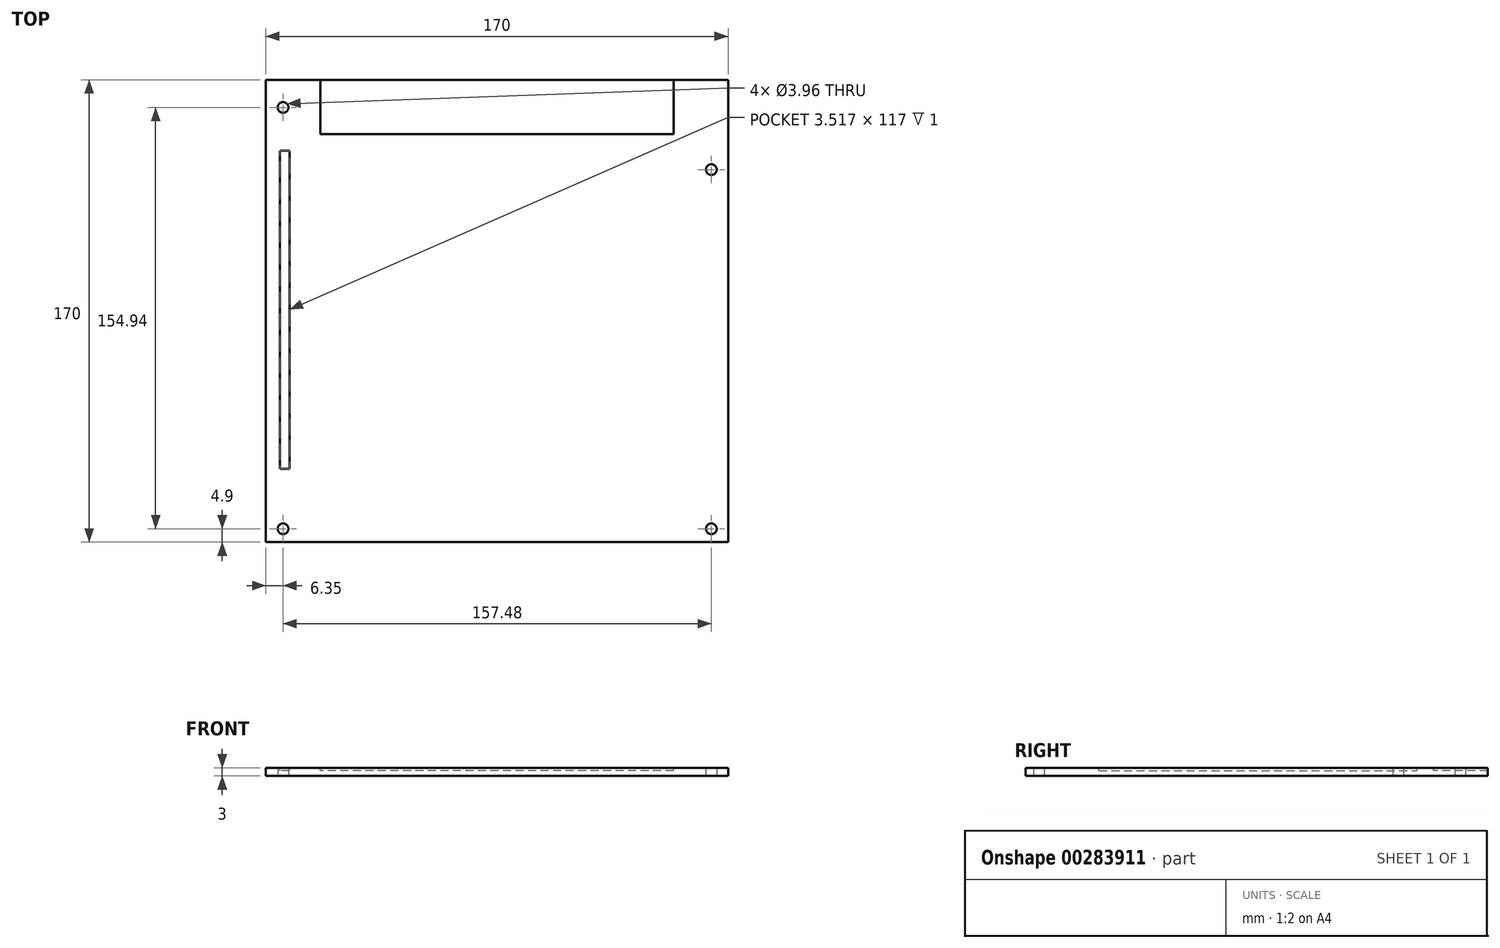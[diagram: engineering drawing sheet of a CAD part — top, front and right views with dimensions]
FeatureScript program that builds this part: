
annotation { "Feature Type Name" : "Feature", "Feature Type Description" : "" }
export const myFeature = defineFeature(function(context is Context, id is Id, definition is map)
    precondition{}
    {
        {
            var Q0;
            Q0=qCreatedBy(makeId("Top.planeOp"),FACE);
            var sketch = newSketch(context, id + "F0", { "sketchPlane" : qUnion([Q0])});
            skLineSegment(sketch, "E0.bottom", {"start": v(85, 85) * mm, "end": v(-85, 85) * mm});
            skLineSegment(sketch, "E0.top", {"start": v(85, -85) * mm, "end": v(-85, -85) * mm});
            skLineSegment(sketch, "E0.left", {"start": v(85, 85) * mm, "end": v(85, -85) * mm});
            skLineSegment(sketch, "E0.right", {"start": v(-85, 85) * mm, "end": v(-85, -85) * mm});
            skPoint(sketch, "E0.middle", {"position": v(0, 0) * mm});
            skCircle(sketch, "E1", {"center": v(-78.65, 74.84) * mm, "radius": 1.98 * mm});
            skCircle(sketch, "E2", {"center": v(78.83, 51.98) * mm, "radius": 1.98 * mm});
            skCircle(sketch, "E3", {"center": v(-78.65, -80.1) * mm, "radius": 1.98 * mm});
            skCircle(sketch, "E4", {"center": v(78.83, -80.1) * mm, "radius": 1.98 * mm});
            skSolve(sketch);
        }
        {
            var Q0;
            Q0 = qSketchRegion(id + "F0", true);
            extrude(context, id + "F1", {"entities" : qUnion([Q0]), "depth" : 3 * mm});
        }
        {
            var Q0;
            Q0=makeQuery(id+"F1.opExtrude","CAP_FACE",FACE,{"disambiguationData":[OSD([sQuery(id+"F0.wireOp",EDGE,"E0.bottom"),sQuery(id+"F0.wireOp",EDGE,"E0.top"),sQuery(id+"F0.wireOp",EDGE,"E0.left"),sQuery(id+"F0.wireOp",EDGE,"E0.right"),sQuery(id+"F0.wireOp",EDGE,"E1"),sQuery(id+"F0.wireOp",EDGE,"E2"),sQuery(id+"F0.wireOp",EDGE,"E3"),sQuery(id+"F0.wireOp",EDGE,"E4")])],"isStart":false});
            var sketch = newSketch(context, id + "F2", { "sketchPlane" : qUnion([Q0])});
            skLineSegment(sketch, "E5.bottom", {"start": v(65, 85) * mm, "end": v(-65, 85) * mm});
            skLineSegment(sketch, "E5.top", {"start": v(65, 65) * mm, "end": v(-65, 65) * mm});
            skLineSegment(sketch, "E5.left", {"start": v(65, 85) * mm, "end": v(65, 65) * mm});
            skLineSegment(sketch, "E5.right", {"start": v(-65, 85) * mm, "end": v(-65, 65) * mm});
            skSolve(sketch);
        }
        {
            var Q0;
            Q0 = qSketchRegion(id + "F2", true);
            extrude(context, id + "F3", {"entities" : qUnion([Q0]), "operationType" : NewBodyOperationType.REMOVE, "oppositeDirection" : true, "depth" : 1 * mm});
        }
        {
            var Q0;
            Q0=makeQuery(id+"F1.opExtrude","CAP_FACE",FACE,{"disambiguationData":[OSD([sQuery(id+"F0.wireOp",EDGE,"E0.bottom"),sQuery(id+"F0.wireOp",EDGE,"E0.top"),sQuery(id+"F0.wireOp",EDGE,"E0.left"),sQuery(id+"F0.wireOp",EDGE,"E0.right"),sQuery(id+"F0.wireOp",EDGE,"E1"),sQuery(id+"F0.wireOp",EDGE,"E2"),sQuery(id+"F0.wireOp",EDGE,"E3"),sQuery(id+"F0.wireOp",EDGE,"E4")])],"isStart":false});
            var sketch = newSketch(context, id + "F4", { "sketchPlane" : qUnion([Q0])});
            skLineSegment(sketch, "E6.bottom", {"start": v(-79.8, 58.97) * mm, "end": v(-76.28, 58.97) * mm});
            skLineSegment(sketch, "E6.top", {"start": v(-79.8, -58.03) * mm, "end": v(-76.28, -58.03) * mm});
            skLineSegment(sketch, "E6.left", {"start": v(-79.8, 58.97) * mm, "end": v(-79.8, -58.03) * mm});
            skLineSegment(sketch, "E6.right", {"start": v(-76.28, 58.97) * mm, "end": v(-76.28, -58.03) * mm});
            skSolve(sketch);
        }
        {
            var Q0;
            Q0 = qSketchRegion(id + "F4", true);
            var Q1;
            Q1=makeQuery(id+"F3.boolean.opBoolean","COPY",FACE,{"derivedFrom":makeQuery(id+"F3.opExtrude","CAP_FACE",FACE,{"disambiguationData":[OSD([sQuery(id+"F2.wireOp",EDGE,"E5.bottom"),sQuery(id+"F2.wireOp",EDGE,"E5.top"),sQuery(id+"F2.wireOp",EDGE,"E5.left"),sQuery(id+"F2.wireOp",EDGE,"E5.right")])],"isStart":false})});
            extrude(context, id + "F5", {"entities" : qUnion([Q0]), "operationType" : NewBodyOperationType.REMOVE, "endBound" : BoundingType.UP_TO_SURFACE, "oppositeDirection" : true, "endBoundEntityFace" : qUnion([Q1]), "depth" : 0.5 * mm});
        }
    });
